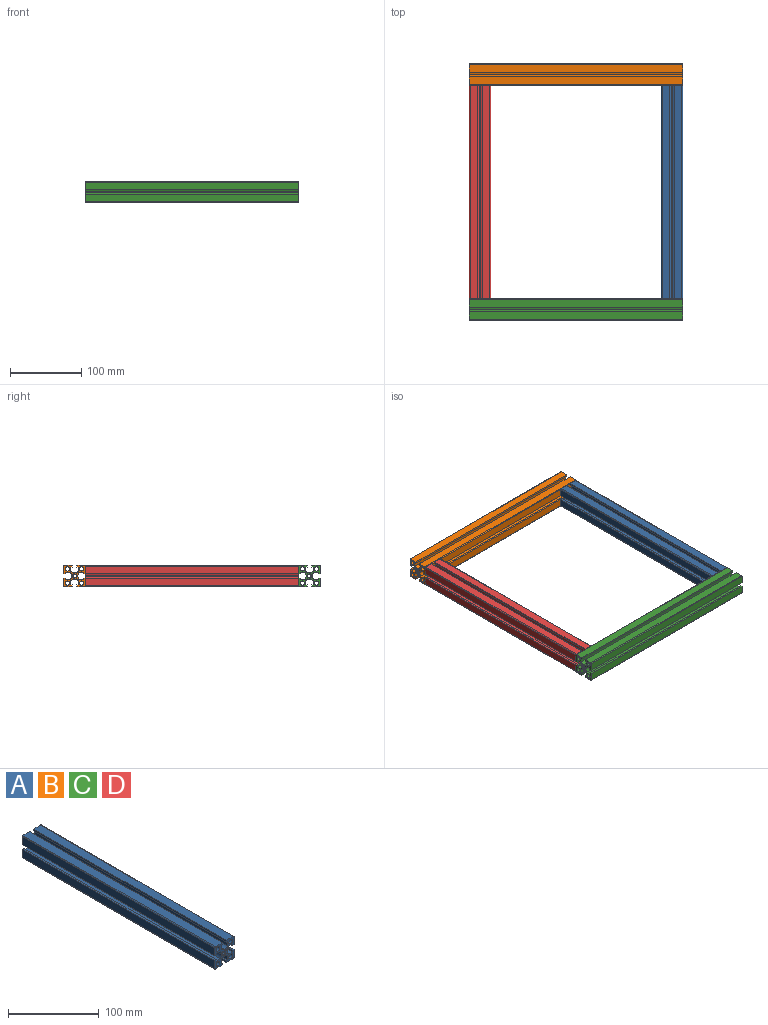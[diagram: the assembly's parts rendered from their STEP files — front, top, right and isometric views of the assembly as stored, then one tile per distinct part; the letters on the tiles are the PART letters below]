
ASSEMBLY  parts=4 mates=9
PART A: 74 faces, bbox 30x300x30 mm
  f0: plane 300x2.5mm, normal (-1,0,0), area 750mm2, adj f1,f67,f68,f69
  f1: plane 300x10.85mm, normal (0,0,-1), area 3255mm2, adj f0,f68,f69,f70
  f2: plane 300x10.85mm, normal (1,0,0), area 3255mm2, adj f3,f68,f69,f70
  f3: plane 300x2.5mm, normal (0,0,1), area 750mm2, adj f2,f4,f68,f69
  f4: plane 300x2mm, normal (-1,0,0), area 600mm2, adj f3,f5,f68,f69
  f5: plane 300x5.95mm, normal (0,0,1), area 1785.7mm2, adj f4,f6,f68,f69
  f6: cylinder r=7.5mm len=300mm, axis (0,-1,0), area 1658mm2, adj f5,f7,f68,f69
  f7: plane 300x0.3mm, normal (0.45,0,0.9), area 101mm2, adj f6,f8,f68,f69
  f8: plane 300x0.3mm, normal (0.45,0,-0.9), area 101mm2, adj f7,f9,f68,f69
  f9: cylinder r=7.5mm len=300mm, axis (0,-1,0), area 1658mm2, adj f8,f10,f68,f69
  f10: plane 300x5.95mm, normal (0,0,-1), area 1785.7mm2, adj f9,f11,f68,f69
  f11: plane 300x2mm, normal (-1,0,0), area 600mm2, adj f10,f12,f68,f69
  f12: plane 300x2.5mm, normal (0,0,-1), area 750mm2, adj f11,f13,f68,f69
  f13: plane 300x10.85mm, normal (1,0,0), area 3255mm2, adj f12,f68,f69,f71
  f14: plane 300x10.85mm, normal (0,0,1), area 3255mm2, adj f15,f68,f69,f71
  f15: plane 300x2.5mm, normal (-1,0,0), area 750mm2, adj f14,f16,f68,f69
  f16: plane 300x2mm, normal (0,0,-1), area 600mm2, adj f15,f17,f68,f69
  f17: plane 300x5.95mm, normal (-1,0,0), area 1785.7mm2, adj f16,f18,f68,f69
  f18: cylinder r=7.5mm len=300mm, axis (0,-1,0), area 1658mm2, adj f17,f19,f68,f69
  f19: plane 300x0.3mm, normal (-0.9,0,0.45), area 101mm2, adj f18,f20,f68,f69
  f20: plane 300x0.3mm, normal (0.9,0,0.45), area 101mm2, adj f19,f21,f68,f69
  f21: cylinder r=7.5mm len=300mm, axis (0,-1,0), area 1658mm2, adj f20,f22,f68,f69
  f22: plane 300x5.95mm, normal (1,0,0), area 1785.7mm2, adj f21,f23,f68,f69
  f23: plane 300x2mm, normal (0,0,-1), area 600mm2, adj f22,f24,f68,f69
  f24: plane 300x2.5mm, normal (1,0,0), area 750mm2, adj f23,f25,f68,f69
  f25: plane 300x10.85mm, normal (0,0,1), area 3255mm2, adj f24,f68,f69,f72
  f26: plane 300x10.85mm, normal (-1,0,0), area 3255mm2, adj f27,f68,f69,f72
  f27: plane 300x2.5mm, normal (0,0,-1), area 750mm2, adj f26,f28,f68,f69
  f28: plane 300x2mm, normal (1,0,0), area 600mm2, adj f27,f29,f68,f69
  f29: plane 300x5.95mm, normal (0,0,-1), area 1785.7mm2, adj f28,f30,f68,f69
  f30: cylinder r=7.5mm len=300mm, axis (0,-1,0), area 1658mm2, adj f29,f31,f68,f69
  f31: plane 300x0.3mm, normal (-0.45,0,-0.9), area 101mm2, adj f30,f32,f68,f69
  f32: plane 300x0.3mm, normal (-0.45,0,0.9), area 101mm2, adj f31,f33,f68,f69
  f33: cylinder r=7.5mm len=300mm, axis (0,-1,0), area 1658mm2, adj f32,f34,f68,f69
  f34: plane 300x5.95mm, normal (0,0,1), area 1785.7mm2, adj f33,f35,f68,f69
  f35: plane 300x2mm, normal (1,0,0), area 600mm2, adj f34,f36,f68,f69
  f36: plane 300x2.5mm, normal (0,0,1), area 750mm2, adj f35,f37,f68,f69
  f37: plane 300x10.85mm, normal (-1,0,0), area 3255mm2, adj f36,f68,f69,f73
  f38: plane 300x10.85mm, normal (0,0,-1), area 3255mm2, adj f39,f68,f69,f73
  f39: plane 300x2.5mm, normal (1,0,0), area 750mm2, adj f38,f40,f68,f69
  f40: plane 300x2mm, normal (0,0,1), area 600mm2, adj f39,f41,f68,f69
  f41: plane 300x5.95mm, normal (1,0,0), area 1785.7mm2, adj f40,f42,f68,f69
  f42: cylinder r=7.5mm len=300mm, axis (0,-1,0), area 1658mm2, adj f41,f43,f68,f69
  f43: plane 300x0.3mm, normal (0.9,0,-0.45), area 101mm2, adj f42,f44,f68,f69
  f44: plane 300x0.3mm, normal (-0.9,0,-0.45), area 101mm2, adj f43,f45,f68,f69
  f45: cylinder r=7.5mm len=300mm, axis (0,-1,0), area 1658mm2, adj f44,f46,f68,f69
  f46: plane 300x5.95mm, normal (-1,0,0), area 1785.7mm2, adj f45,f67,f68,f69
  f47: cylinder r=3.5mm len=300mm, axis (0,-1,0), area 361.8mm2, adj f48,f66,f68,f69
  f48: plane 300x0.72mm, normal (-0.71,0,0.71), area 306.4mm2, adj f47,f49,f68,f69
  f49: cylinder r=2.5mm len=300mm, axis (0,-1,0), area 814.5mm2, adj f48,f50,f68,f69
  f50: plane 300x0.72mm, normal (-0.71,0,-0.71), area 306.4mm2, adj f49,f51,f68,f69
  f51: cylinder r=3.5mm len=300mm, axis (0,-1,0), area 361.8mm2, adj f50,f52,f68,f69
  f52: plane 300x0.72mm, normal (0.71,0,0.71), area 306.4mm2, adj f51,f53,f68,f69
  f53: cylinder r=2.5mm len=300mm, axis (0,-1,0), area 814.5mm2, adj f52,f54,f68,f69
  f54: plane 300x0.72mm, normal (-0.71,0,0.71), area 306.4mm2, adj f53,f55,f68,f69
  f55: cylinder r=3.5mm len=300mm, axis (0,-1,0), area 361.8mm2, adj f54,f56,f68,f69
  f56: plane 300x0.72mm, normal (0.71,0,-0.71), area 306.4mm2, adj f55,f57,f68,f69
  f57: cylinder r=2.5mm len=300mm, axis (0,-1,0), area 814.5mm2, adj f56,f58,f68,f69
  f58: plane 300x0.72mm, normal (0.71,0,0.71), area 306.4mm2, adj f57,f59,f68,f69
  f59: cylinder r=3.5mm len=300mm, axis (0,-1,0), area 361.8mm2, adj f58,f60,f68,f69
  f60: plane 300x0.72mm, normal (-0.71,0,-0.71), area 306.4mm2, adj f59,f61,f68,f69
  f61: cylinder r=2.5mm len=300mm, axis (0,-1,0), area 814.5mm2, adj f60,f66,f68,f69
  f62: cylinder r=3mm len=300mm, axis (0,-1,0), area 5654.9mm2, adj f68,f69
  f63: cylinder r=3mm len=300mm, axis (0,-1,0), area 5654.9mm2, adj f68,f69
  f64: cylinder r=3mm len=300mm, axis (0,-1,0), area 5654.9mm2, adj f68,f69
  f65: cylinder r=3mm len=300mm, axis (0,-1,0), area 5654.9mm2, adj f68,f69
  f66: plane 300x0.72mm, normal (0.71,0,-0.71), area 306.4mm2, adj f47,f61,f68,f69
  f67: plane 300x2mm, normal (0,0,1), area 600mm2, adj f0,f46,f68,f69
  f68: plane 30x30mm, normal (0,1,0), area 395.2mm2, adj f0,f1,f2,f3,f4,f5,f6,f7
  f69: plane 30x30mm, normal (0,-1,0), area 395.2mm2, adj f0,f1,f2,f3,f4,f5,f6,f7
  f70: cylinder r=1mm len=300mm, axis (0,1,0), area 471.2mm2, adj f1,f2,f68,f69
  f71: cylinder r=1mm len=300mm, axis (0,-1,0), area 471.2mm2, adj f13,f14,f68,f69
  f72: cylinder r=1mm len=300mm, axis (0,1,0), area 471.2mm2, adj f25,f26,f68,f69
  f73: cylinder r=1mm len=300mm, axis (0,-1,0), area 471.2mm2, adj f37,f38,f68,f69
PART B: same geometry as A
PART C: same geometry as A
PART D: same geometry as A
PLACE A t=(389.79,247.37,107.14)mm
PLACE B rot(axis=(0,0,1),90deg) t=(404.79,562.37,107.14)mm
PLACE C rot(axis=(0,0,1),90deg) t=(404.79,232.37,107.14)mm
PLACE D rot(axis=(0,0,1),180deg) t=(119.79,547.37,107.14)mm fixed
MATE planar D.f47 <-> A.f59  axis (0,-1,0) through (119.79,247.37,107.14)mm
MATE planar B.f59 <-> A.f13  axis (1,0,0) through (404.79,562.37,107.14)mm
MATE planar D.f25 <-> B.f25  axis (0,0,1) through (128.37,397.37,122.14)mm
MATE planar A.f47 <-> B.f26  axis (0,1,0) through (389.79,547.37,107.14)mm
MATE planar C.f63 <-> A.f13  axis (1,0,0) through (404.79,242.37,117.14)mm
MATE parallel B.f13 <-> C.f26  axis (0,1,0) through (254.79,577.37,115.72)mm
MATE planar C.f14 <-> A.f14  axis (0,0,1) through (254.79,240.94,122.14)mm
MATE planar D.f25 <-> A.f14  axis (0,0,1) through (128.37,397.37,122.14)mm
MATE planar C.f13 <-> A.f62  axis (0,1,0) through (254.79,247.37,115.72)mm
